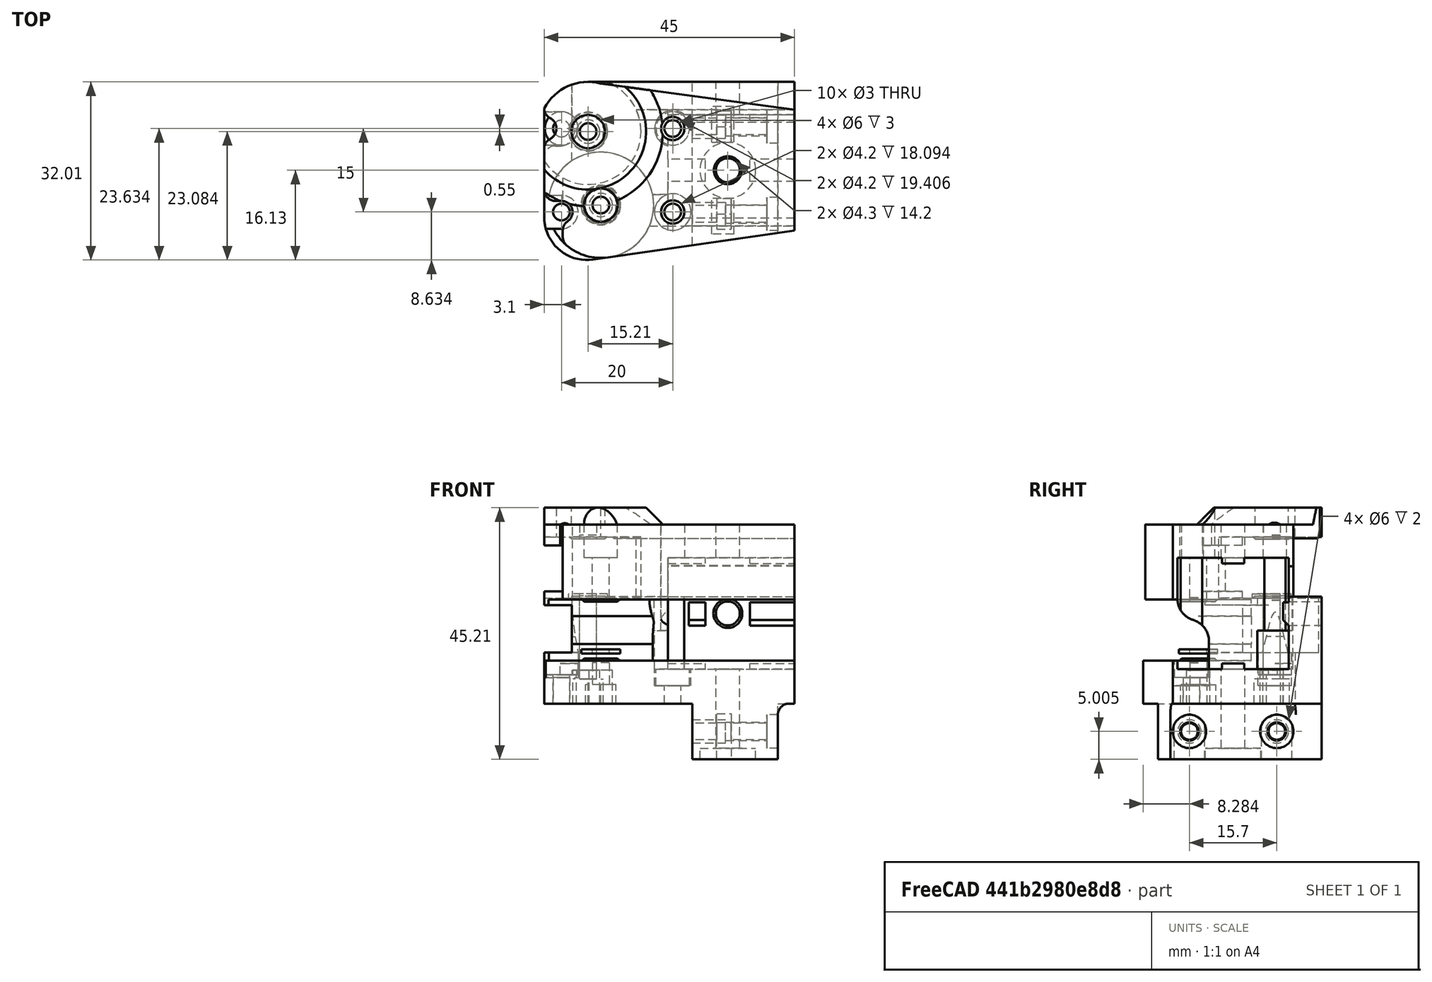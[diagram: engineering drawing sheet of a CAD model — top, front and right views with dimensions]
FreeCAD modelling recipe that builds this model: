
FCSTD DOCUMENT  (FreeCAD 0.18R16146 (Git))
Label: carrier-left-2
License: All rights reserved
LicenseURL: http://en.wikipedia.org/wiki/All_rights_reserved
objects: Part::Cylinder×22, Part::Cut×13, Part::MultiFuse×12, Part::Box×10, Part::Chamfer×6, Part::Feature×6
note: 69 computed .brp shape members not serialized (recipe doc carries the construction recipe); baked Part::Feature solids carry a one-line shape summary decoded from their .brp

FEATURE [Part::Box] Box  label="Cube"
  AttacherType = Attacher::AttachEngine3D
  Height = 20
  Length = 70
  Placement = pos=(2.13,-5.55,16.2) rot=(0,0,1;0rad)
  Width = 20
FEATURE [Part::Cylinder] Cylinder
  Angle = 360
  AttacherType = Attacher::AttachEngine3D
  Height = 6
  Placement = pos=(12.9,4.45,36.2) rot=(0,0,1;0rad)
  Radius = 2.6
FEATURE [Part::Cylinder] Cylinder001
  Angle = 360
  AttacherType = Attacher::AttachEngine3D
  Height = 14.2
  Placement = pos=(12.9,4.45,2) rot=(0,0,1;0rad)
  Radius = 2.6
FEATURE [Part::Cylinder] Cylinder002
  Angle = 360
  AttacherType = Attacher::AttachEngine3D
  Height = 14.2
  Placement = pos=(12.9,4.45,2) rot=(0,0,1;0rad)
  Radius = 2.15
FEATURE [Part::Cylinder] Cylinder003
  Angle = 360
  AttacherType = Attacher::AttachEngine3D
  Height = 6
  Placement = pos=(12.9,4.45,36.2) rot=(0,0,1;0rad)
  Radius = 2.15
FEATURE [Part::Cylinder] Cylinder004
  Angle = 360
  AttacherType = Attacher::AttachEngine3D
  Height = 5.88
  Placement = pos=(12.9,14.45,26.2) rot=(-1,0,0;1.5708rad)
  Radius = 2.6
FEATURE [Part::Cylinder] Cylinder005
  Angle = 360
  AttacherType = Attacher::AttachEngine3D
  Height = 5.88
  Placement = pos=(12.9,14.45,26.2) rot=(-1,0,0;1.5708rad)
  Radius = 2.15
FEATURE [Part::Box] Box001  label="Cube001"
  AttacherType = Attacher::AttachEngine3D
  Height = 1.1
  Length = 7
  Placement = pos=(1.9,2.45,16.1) rot=(0,0,1;0rad)
  Width = 4
FEATURE [Part::Box] Box002  label="Cube002"
  AttacherType = Attacher::AttachEngine3D
  Height = 1.1
  Length = 8
  Placement = pos=(16.9,2.45,16.1) rot=(0,0,1;0rad)
  Width = 4
FEATURE [Part::Box] Box003  label="Cube003"
  AttacherType = Attacher::AttachEngine3D
  Height = 4.2
  Length = 8
  Placement = pos=(16.9,13.45,24.01) rot=(0,0,1;0rad)
  Width = 1.1
FEATURE [Part::Box] Box004  label="Cube004"
  AttacherType = Attacher::AttachEngine3D
  Height = 4.2
  Length = 3
  Placement = pos=(5.9,13.45,24.01) rot=(0,0,1;0rad)
  Width = 1.1
FEATURE [Part::Chamfer] Chamfer
  Base = -> Box004
  Edges = 1 edges r=1: [Edge9]
FEATURE [Part::Chamfer] Chamfer001
  Base = -> Box003
  Edges = 1 edges r=1: [Edge9]
FEATURE [Part::Box] Box005  label="Cube005"
  AttacherType = Attacher::AttachEngine3D
  Height = 1.1
  Length = 7
  Placement = pos=(1.9,2.45,35.2) rot=(0,0,1;0rad)
  Width = 4
FEATURE [Part::Box] Box006  label="Cube006"
  AttacherType = Attacher::AttachEngine3D
  Height = 1.1
  Length = 8
  Placement = pos=(16.9,2.45,35.2) rot=(0,0,1;0rad)
  Width = 4
FEATURE [Part::MultiFuse] Fusion  label="M4-channel"
  Shapes = -> [Box001,Chamfer001,Box002,Box006,Box005,Chamfer]
FEATURE [Part::Cut] Cut004
  Base = -> Cylinder
  Tool = -> Cylinder003
FEATURE [Part::Cut] Cut005
  Base = -> Cylinder001
  Tool = -> Cylinder002
FEATURE [Part::Cut] Cut006
  Base = -> Cylinder004
  Tool = -> Cylinder005
FEATURE [Part::MultiFuse] Fusion002  label="bolt-adapter"
  Shapes = -> [Cut004,Cut006,Cut005]
FEATURE [Part::Feature] Part__Feature142  label="std-left"
  Placement = pos=(8,-213,-461.82) rot=(1,0,0;1.5708rad)
  shape: bbox 47.27 x 33.44 x 45.2 mm, 159 faces (baked)
FEATURE [Part::Cut] Cut
  Base = -> Part__Feature142
  Tool = -> Box
FEATURE [Part::MultiFuse] Fusion003
  Shapes = -> [Cut,Fusion]
FEATURE [Part::MultiFuse] Fusion004
  Shapes = -> [Fusion003,Fusion002]
FEATURE [Part::Cylinder] Cylinder006
  Angle = 360
  AttacherType = Attacher::AttachEngine3D
  Height = 11
  Placement = pos=(-12.21,11.4,28.95) rot=(0,0,1;0rad)
  Radius = 9.5
FEATURE [Part::Cylinder] Cylinder007
  Angle = 360
  AttacherType = Attacher::AttachEngine3D
  Height = 0.75
  Placement = pos=(-12.21,11.4,28.95) rot=(0,0,1;0rad)
  Radius = 3.5
FEATURE [Part::Cut] Cut007
  Base = -> Fusion004
  Tool = -> Cylinder006
FEATURE [Part::Cylinder] Cylinder008
  Angle = 360
  AttacherType = Attacher::AttachEngine3D
  Height = 0.75
  Placement = pos=(-12.21,11.4,28.95) rot=(0,0,1;0rad)
  Radius = 1.5
FEATURE [Part::Cylinder] Cylinder009
  Angle = 360
  AttacherType = Attacher::AttachEngine3D
  Height = 0.75
  Placement = pos=(-9.92,-1.8,19) rot=(0,0,1;0rad)
  Radius = 3.5
FEATURE [Part::Cylinder] Cylinder010
  Angle = 360
  AttacherType = Attacher::AttachEngine3D
  Height = 3
  Placement = pos=(-9.92,-1.8,25.7) rot=(0,0,1;0rad)
  Radius = 9.5
FEATURE [Part::Cylinder] Cylinder011
  Angle = 360
  AttacherType = Attacher::AttachEngine3D
  Height = 3
  Placement = pos=(-9.92,-1.8,17.7) rot=(0,0,1;0rad)
  Radius = 9.5
FEATURE [Part::Cylinder] Cylinder012
  Angle = 360
  AttacherType = Attacher::AttachEngine3D
  Height = 0.75
  Placement = pos=(-9.92,-1.8,19) rot=(0,0,1;0rad)
  Radius = 1.5
FEATURE [Part::Cut] Cut008002005
  Base = -> Cylinder007
  Tool = -> Cylinder008
FEATURE [Part::Feature] Cut008002005001  label="Cut008002006"
  Placement = pos=(0,0,10.6) rot=(0,0,1;0rad)
  shape: bbox 7 x 7 x 0.75 mm, 4 faces (baked)
FEATURE [Part::Feature] Cut008002005003  label="Cut008002009"
  Placement = pos=(0,0,-0.35) rot=(0,0,1;0rad)
  shape: bbox 7 x 7 x 0.75 mm, 4 faces (baked)
FEATURE [Part::Chamfer] Chamfer002
  Base = -> Cut008002005001
  Edges = 1 edges r=0.5: [Edge3]
FEATURE [Part::Chamfer] Chamfer003
  Base = -> Cut008002005003
  Edges = 1 edges r=0.5: [Edge1]
FEATURE [Part::Cut] Cut008002005004
  Base = -> Cylinder009
  Tool = -> Cylinder012
FEATURE [Part::Feature] Cut008002005004001  label="Cut008002005005"
  Placement = pos=(0,0,9.3) rot=(0,0,1;0rad)
  shape: bbox 7 x 7 x 0.75 mm, 4 faces (baked)
FEATURE [Part::Feature] Cut008002005004002  label="Cut008002005006"
  Placement = pos=(0,0,-1.65) rot=(0,0,1;0rad)
  shape: bbox 7 x 7 x 0.75 mm, 4 faces (baked)
FEATURE [Part::Chamfer] Chamfer004
  Base = -> Cut008002005004001
  Edges = 1 edges r=0.5: [Edge3]
FEATURE [Part::Chamfer] Chamfer005
  Base = -> Cut008002005004002
  Edges = 1 edges r=0.5: [Edge1]
FEATURE [Part::Box] Box007  label="Cube007"
  AttacherType = Attacher::AttachEngine3D
  Height = 10
  Length = 10
  Placement = pos=(-25.1,5.95,21.7) rot=(0,0,1;0rad)
  Width = 10
FEATURE [Part::Cut] Cut008002005004003
  Base = -> Chamfer003
  Tool = -> Box007
FEATURE [Part::MultiFuse] Fusion005
  Shapes = -> [Cut008002005004003,Chamfer005,Chamfer004,Chamfer002]
FEATURE [Part::Cut] Cut008002005004004
  Base = -> Cut007
  Tool = -> Cylinder011
FEATURE [Part::Cut] Cut008002005004005
  Base = -> Cut008002005004004
  Tool = -> Cylinder010
FEATURE [Part::MultiFuse] Fusion006  label="std-r1"
  Shapes = -> [Cut008002005004005,Fusion005]
FEATURE [Part::Cylinder] Cylinder013
  Angle = 360
  AttacherType = Attacher::AttachEngine3D
  Height = 6
  Placement = pos=(-9.92,-1.8,10) rot=(0,0,1;0rad)
  Radius = 3.3
FEATURE [Part::Cylinder] Cylinder014
  Angle = 360
  AttacherType = Attacher::AttachEngine3D
  Height = 6
  Placement = pos=(-12.21,11.4,10.01) rot=(0,0,1;0rad)
  Radius = 3.3
FEATURE [Part::Feature] Fusion006_solid  label="std-r1 (Solid)"
  shape: bbox 47.27 x 33.44 x 45.2 mm, 235 faces (baked)
FEATURE [Part::Cylinder] Cylinder015
  Angle = 360
  AttacherType = Attacher::AttachEngine3D
  Height = 6
  Placement = pos=(-12.21,11.4,10.01) rot=(0,0,1;0rad)
  Radius = 2.1
FEATURE [Part::Cylinder] Cylinder016
  Angle = 360
  AttacherType = Attacher::AttachEngine3D
  Height = 6
  Placement = pos=(-9.92,-1.8,10) rot=(0,0,1;0rad)
  Radius = 2.1
FEATURE [Part::MultiFuse] Fusion007
  Shapes = -> [Fusion006_solid,Cylinder014,Cylinder013]
FEATURE [Part::MultiFuse] Fusion008
  Shapes = -> [Cylinder016,Cylinder015]
FEATURE [Part::Cut] Cut008002005004006
  Base = -> Fusion007
  Tool = -> Fusion008
FEATURE [Part::Cylinder] Cylinder017
  Angle = 360
  AttacherType = Attacher::AttachEngine3D
  Height = 2
  Placement = pos=(-17,11.96,15.2) rot=(0,0,1;0rad)
  Radius = 3
FEATURE [Part::Cut] Cut008002005004007  label="insert-r1"
  Base = -> Cut008002005004006
  Tool = -> Cylinder017
FEATURE [Part::Cylinder] Cylinder018
  Angle = 360
  AttacherType = Attacher::AttachEngine3D
  Height = 6
  Placement = pos=(6.5,-3.4,5) rot=(0,1,0;1.5708rad)
  Radius = 2.1
FEATURE [Part::Cylinder] Cylinder019
  Angle = 360
  AttacherType = Attacher::AttachEngine3D
  Height = 6
  Placement = pos=(6.5,12.3,5) rot=(0,1,0;1.5708rad)
  Radius = 2.1
FEATURE [Part::Box] Box008  label="Cube008"
  AttacherType = Attacher::AttachEngine3D
  Height = 9
  Length = 4
  Placement = pos=(10,-7,0) rot=(0,0,1;0rad)
  Width = 6.4
FEATURE [Part::Box] Box009  label="Cube009"
  AttacherType = Attacher::AttachEngine3D
  Height = 9
  Length = 4
  Placement = pos=(10,9.5,0) rot=(0,0,1;0rad)
  Width = 6.4
FEATURE [Part::MultiFuse] Fusion009
  Shapes = -> [Box009,Box008,Cut008002005004007]
FEATURE [Part::Cylinder] Cylinder020
  Angle = 360
  AttacherType = Attacher::AttachEngine3D
  Height = 32
  Placement = pos=(6.5,-3.4,5) rot=(0,1,0;1.5708rad)
  Radius = 1.65
FEATURE [Part::Cylinder] Cylinder021
  Angle = 360
  AttacherType = Attacher::AttachEngine3D
  Height = 32
  Placement = pos=(6.5,12.3,5) rot=(0,1,0;1.5708rad)
  Radius = 1.65
FEATURE [Part::MultiFuse] Fusion010
  Shapes = -> [Cylinder018,Cylinder019]
FEATURE [Part::MultiFuse] Fusion011
  Shapes = -> [Cylinder021,Cylinder020]
FEATURE [Part::MultiFuse] Fusion012
  Shapes = -> [Fusion011,Fusion010]
FEATURE [Part::Cut] Cut008002005004008
  Base = -> Fusion009
  Tool = -> Fusion012
